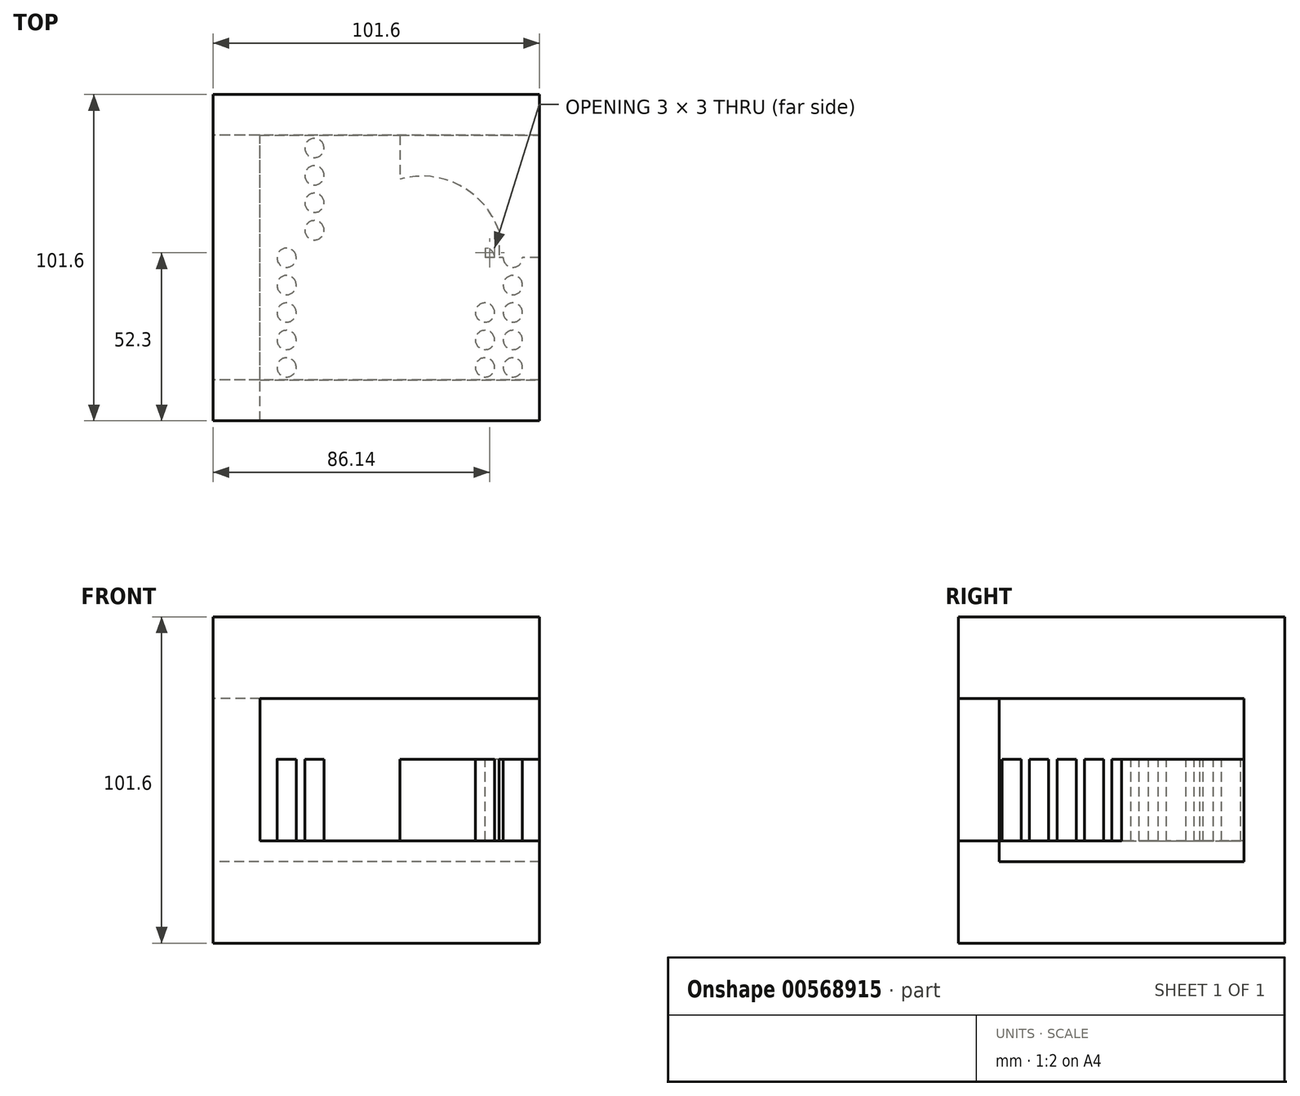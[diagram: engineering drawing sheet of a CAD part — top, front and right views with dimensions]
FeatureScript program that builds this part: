
annotation { "Feature Type Name" : "Feature", "Feature Type Description" : "" }
export const myFeature = defineFeature(function(context is Context, id is Id, definition is map)
    precondition{}
    {
        {
            var Q0;
            Q0=qCreatedBy(makeId("Front.planeOp"),FACE);
            var sketch = newSketch(context, id + "F0", { "sketchPlane" : qUnion([Q0])});
            skLineSegment(sketch, "E0.bottom", {"start": v(-50.8, 50.8) * mm, "end": v(50.8, 50.8) * mm});
            skLineSegment(sketch, "E0.top", {"start": v(-50.8, -50.8) * mm, "end": v(50.8, -50.8) * mm});
            skLineSegment(sketch, "E0.left", {"start": v(-50.8, 50.8) * mm, "end": v(-50.8, -50.8) * mm});
            skLineSegment(sketch, "E0.right", {"start": v(50.8, 50.8) * mm, "end": v(50.8, -50.8) * mm});
            skPoint(sketch, "E0.middle", {"position": v(0, 0) * mm});
            skSolve(sketch);
        }
        {
            var Q0;
            Q0=makeQuery(id+"F0.imprint","IMPRINT",FACE,{"disambiguationData":[TD([[makeQuery(id+"F0.imprint","IMPRINT",EDGE,{"derivedFrom":sQuery(id+"F0.wireOp",EDGE,"E0.bottom")}),-1.0]])]});
            extrude(context, id + "F1", {"entities" : qUnion([Q0]), "endBound" : BoundingType.SYMMETRIC, "depth" : 101.6 * mm, "offsetDistance" : 25.4 * mm});
        }
        {
            var Q0;
            Q0=qCreatedBy(makeId("Right.planeOp"),FACE);
            var sketch = newSketch(context, id + "F2", { "sketchPlane" : qUnion([Q0])});
            skLineSegment(sketch, "E1.bottom", {"start": v(-38.1, 25.4) * mm, "end": v(38.1, 25.4) * mm});
            skLineSegment(sketch, "E1.top", {"start": v(-38.1, -25.4) * mm, "end": v(38.1, -25.4) * mm});
            skLineSegment(sketch, "E1.left", {"start": v(-38.1, 25.4) * mm, "end": v(-38.1, -25.4) * mm});
            skLineSegment(sketch, "E1.right", {"start": v(38.1, 25.4) * mm, "end": v(38.1, -25.4) * mm});
            skPoint(sketch, "E1.middle", {"position": v(0, 0) * mm});
            skSolve(sketch);
        }
        {
            var Q0;
            Q0=makeQuery(id+"F2.imprint","IMPRINT",FACE,{"disambiguationData":[TD([[makeQuery(id+"F2.imprint","IMPRINT",EDGE,{"derivedFrom":sQuery(id+"F2.wireOp",EDGE,"E1.bottom")}),-1.0]])]});
            extrude(context, id + "F3", {"entities" : qUnion([Q0]), "endBound" : BoundingType.SYMMETRIC, "depth" : 101.6 * mm, "offsetDistance" : 25.4 * mm});
        }
        {
            var Q0;
            Q0=makeQuery(id+"F3.opExtrude","SWEPT_FACE",FACE,{"disambiguationData":[OSD([sQuery(id+"F2.wireOp",EDGE,"E1.right")])]});
            var sketch = newSketch(context, id + "F4", { "sketchPlane" : qUnion([Q0])});
            skLineSegment(sketch, "E2.bottom", {"start": v(36.24, 6.44) * mm, "end": v(-137.84, 6.44) * mm});
            skLineSegment(sketch, "E2.top", {"start": v(36.24, 44.36) * mm, "end": v(-137.84, 44.36) * mm});
            skLineSegment(sketch, "E2.left", {"start": v(36.24, 6.44) * mm, "end": v(36.24, 44.36) * mm});
            skLineSegment(sketch, "E2.right", {"start": v(-137.84, 6.44) * mm, "end": v(-137.84, 44.36) * mm});
            skPoint(sketch, "E2.middle", {"position": v(-50.8, 25.4) * mm});
            skSolve(sketch);
        }
        {
            var Q0;
            {var subQ0=sQuery(id+"F4.wireOp",EDGE,"E2.left");var subQ1=sQuery(id+"F4.wireOp",EDGE,"E2.bottom");var subQ2=makeQuery(id+"F4.imprint","INTERSECT",VERTEX,{"derivedFrom":[subQ1,subQ0]});Q0=makeQuery(id+"F4.imprint","IMPRINT",FACE,{"disambiguationData":[TD([[makeQuery(id+"F4.imprint","IMPRINT",EDGE,{"disambiguationData":[TD([[subQ2,-1.0]])],"derivedFrom":subQ1}),-1.0]])]});}
            extrude(context, id + "F5", {"entities" : qUnion([Q0]), "operationType" : NewBodyOperationType.REMOVE, "oppositeDirection" : true, "depth" : 135.89 * mm, "offsetDistance" : 25.4 * mm});
        }
        {
            var Q0;
            Q0=makeQuery(id+"F5.boolean.opBoolean","COPY",FACE,{"derivedFrom":makeQuery(id+"F5.opExtrude","SWEPT_FACE",FACE,{"disambiguationData":[OSD([sQuery(id+"F4.wireOp",EDGE,"E2.bottom")])]})});
            var sketch = newSketch(context, id + "F6", { "sketchPlane" : qUnion([Q0])});
            skCircle(sketch, "E3", {"center": v(33.84, 25.62) * mm, "radius": 3 * mm});
            skCircle(sketch, "E4", {"center": v(33.84, 17.08) * mm, "radius": 3 * mm});
            skCircle(sketch, "E5", {"center": v(33.84, 8.54) * mm, "radius": 3 * mm});
            skLineSegment(sketch, "E6", {"start": v(38.17, 38.1) * mm, "end": v(38.17, -38.1) * mm});
            skCircle(sketch, "E7.MirrorC", {"center": v(42.5, 25.62) * mm, "radius": 3 * mm});
            skCircle(sketch, "E8.MirrorC", {"center": v(42.5, 17.08) * mm, "radius": 3 * mm});
            skCircle(sketch, "E9.MirrorC", {"center": v(42.5, 8.54) * mm, "radius": 3 * mm});
            skLineSegment(sketch, "E10", {"start": v(50.8, 0) * mm, "end": v(-36.24, 0) * mm});
            skLineSegment(sketch, "E11", {"start": v(33.84, 38.1) * mm, "end": v(33.84, -38.1) * mm});
            skCircle(sketch, "E12.MirrorC", {"center": v(33.84, -8.54) * mm, "radius": 3 * mm});
            skCircle(sketch, "E13.MirrorC", {"center": v(33.84, -17.08) * mm, "radius": 3 * mm});
            skCircle(sketch, "E14.MirrorC", {"center": v(33.84, -25.62) * mm, "radius": 3 * mm});
            skCircle(sketch, "E15.MirrorC", {"center": v(42.5, -25.62) * mm, "radius": 3 * mm});
            skCircle(sketch, "E16.MirrorC", {"center": v(42.5, -17.08) * mm, "radius": 3 * mm});
            skCircle(sketch, "E17.MirrorC", {"center": v(42.5, -8.54) * mm, "radius": 3 * mm});
            skCircle(sketch, "E18", {"center": v(33.84, 0) * mm, "radius": 3 * mm});
            skCircle(sketch, "E19.MirrorC", {"center": v(42.5, 0) * mm, "radius": 3 * mm});
            skLineSegment(sketch, "E20", {"start": v(7.28, 38.1) * mm, "end": v(7.28, -38.1) * mm});
            skCircle(sketch, "E21.MirrorC", {"center": v(-19.28, 25.62) * mm, "radius": 3 * mm});
            skCircle(sketch, "E22.MirrorC", {"center": v(-27.94, 25.62) * mm, "radius": 3 * mm});
            skCircle(sketch, "E23.MirrorC", {"center": v(-19.28, 17.08) * mm, "radius": 3 * mm});
            skCircle(sketch, "E24.MirrorC", {"center": v(-27.94, 17.08) * mm, "radius": 3 * mm});
            skCircle(sketch, "E25.MirrorC", {"center": v(-19.28, 8.54) * mm, "radius": 3 * mm});
            skCircle(sketch, "E26.MirrorC", {"center": v(-27.94, 8.54) * mm, "radius": 3 * mm});
            skCircle(sketch, "E27.MirrorC", {"center": v(-19.28, 0) * mm, "radius": 3 * mm});
            skCircle(sketch, "E28.MirrorC", {"center": v(-27.94, 0) * mm, "radius": 3 * mm});
            skCircle(sketch, "E29.MirrorC", {"center": v(-19.28, -8.54) * mm, "radius": 3 * mm});
            skCircle(sketch, "E30.MirrorC", {"center": v(-27.94, -8.54) * mm, "radius": 3 * mm});
            skCircle(sketch, "E31.MirrorC", {"center": v(-19.28, -17.08) * mm, "radius": 3 * mm});
            skCircle(sketch, "E32.MirrorC", {"center": v(-27.94, -17.08) * mm, "radius": 3 * mm});
            skCircle(sketch, "E33.MirrorC", {"center": v(-19.28, -25.62) * mm, "radius": 3 * mm});
            skCircle(sketch, "E34.MirrorC", {"center": v(-27.94, -25.62) * mm, "radius": 3 * mm});
            skCircle(sketch, "E35", {"center": v(14.2, 0) * mm, "radius": 25.4 * mm});
            skCircle(sketch, "E36", {"center": v(33.84, 34.16) * mm, "radius": 3 * mm});
            skCircle(sketch, "E37.MirrorC", {"center": v(42.5, 34.16) * mm, "radius": 3 * mm});
            skCircle(sketch, "E38.MirrorC", {"center": v(33.84, -34.16) * mm, "radius": 3 * mm});
            skCircle(sketch, "E39.MirrorC", {"center": v(42.5, -34.16) * mm, "radius": 3 * mm});
            skCircle(sketch, "E40.MirrorC", {"center": v(-19.28, 34.16) * mm, "radius": 3 * mm});
            skCircle(sketch, "E41.MirrorC", {"center": v(-27.94, 34.16) * mm, "radius": 3 * mm});
            skCircle(sketch, "E42.MirrorC", {"center": v(-19.28, -34.16) * mm, "radius": 3 * mm});
            skCircle(sketch, "E43.MirrorC", {"center": v(-27.94, -34.16) * mm, "radius": 3 * mm});
            skSolve(sketch);
        }
        {
            var Q0;
            Q0=makeQuery(id+"F6.imprint","IMPRINT",FACE,{"disambiguationData":[TD([[makeQuery(id+"F6.imprint","IMPRINT",EDGE,{"derivedFrom":sQuery(id+"F6.wireOp",EDGE,"E22.MirrorC")}),1.0]])]});
            var Q1;
            Q1=makeQuery(id+"F6.imprint","IMPRINT",FACE,{"disambiguationData":[TD([[makeQuery(id+"F6.imprint","IMPRINT",EDGE,{"derivedFrom":sQuery(id+"F6.wireOp",EDGE,"E21.MirrorC")}),-1.0]])]});
            var Q2;
            Q2=makeQuery(id+"F6.imprint","IMPRINT",FACE,{"disambiguationData":[TD([[makeQuery(id+"F6.imprint","IMPRINT",EDGE,{"derivedFrom":sQuery(id+"F6.wireOp",EDGE,"E24.MirrorC")}),1.0]])]});
            var Q3;
            Q3=makeQuery(id+"F6.imprint","IMPRINT",FACE,{"disambiguationData":[TD([[makeQuery(id+"F6.imprint","IMPRINT",EDGE,{"derivedFrom":sQuery(id+"F6.wireOp",EDGE,"E23.MirrorC")}),-1.0]])]});
            var Q4;
            Q4=makeQuery(id+"F6.imprint","IMPRINT",FACE,{"disambiguationData":[TD([[makeQuery(id+"F6.imprint","IMPRINT",EDGE,{"derivedFrom":sQuery(id+"F6.wireOp",EDGE,"E26.MirrorC")}),1.0]])]});
            var Q5;
            Q5=makeQuery(id+"F6.imprint","IMPRINT",FACE,{"disambiguationData":[TD([[makeQuery(id+"F6.imprint","IMPRINT",EDGE,{"derivedFrom":sQuery(id+"F6.wireOp",EDGE,"E25.MirrorC")}),-1.0]])]});
            var Q6;
            {var subQ0=sQuery(id+"F6.wireOp",EDGE,"E28.MirrorC");var subQ1=sQuery(id+"F6.wireOp",EDGE,"E10");var subQ2=makeQuery(id+"F6.imprint","INTERSECT",VERTEX,{"disambiguationData":[OD(0.0)],"derivedFrom":[subQ1,subQ0]});Q6=makeQuery(id+"F6.imprint","IMPRINT",FACE,{"disambiguationData":[TD([[makeQuery(id+"F6.imprint","IMPRINT",EDGE,{"disambiguationData":[TD([[subQ2,-1.0]])],"derivedFrom":subQ1}),-1.0]])]});}
            var Q7;
            {var subQ0=sQuery(id+"F6.wireOp",EDGE,"E27.MirrorC");var subQ1=sQuery(id+"F6.wireOp",EDGE,"E10");var subQ2=makeQuery(id+"F6.imprint","INTERSECT",VERTEX,{"disambiguationData":[OD(0.0)],"derivedFrom":[subQ1,subQ0]});Q7=makeQuery(id+"F6.imprint","IMPRINT",FACE,{"disambiguationData":[TD([[makeQuery(id+"F6.imprint","IMPRINT",EDGE,{"disambiguationData":[TD([[subQ2,-1.0]])],"derivedFrom":subQ1}),1.0]])]});}
            var Q8;
            {var subQ0=sQuery(id+"F6.wireOp",EDGE,"E27.MirrorC");var subQ1=sQuery(id+"F6.wireOp",EDGE,"E10");var subQ2=makeQuery(id+"F6.imprint","INTERSECT",VERTEX,{"disambiguationData":[OD(0.0)],"derivedFrom":[subQ1,subQ0]});Q8=makeQuery(id+"F6.imprint","IMPRINT",FACE,{"disambiguationData":[TD([[makeQuery(id+"F6.imprint","IMPRINT",EDGE,{"disambiguationData":[TD([[subQ2,-1.0]])],"derivedFrom":subQ1}),-1.0]])]});}
            var Q9;
            {var subQ0=sQuery(id+"F6.wireOp",EDGE,"E28.MirrorC");var subQ1=sQuery(id+"F6.wireOp",EDGE,"E10");var subQ2=makeQuery(id+"F6.imprint","INTERSECT",VERTEX,{"disambiguationData":[OD(0.0)],"derivedFrom":[subQ1,subQ0]});Q9=makeQuery(id+"F6.imprint","IMPRINT",FACE,{"disambiguationData":[TD([[makeQuery(id+"F6.imprint","IMPRINT",EDGE,{"disambiguationData":[TD([[subQ2,-1.0]])],"derivedFrom":subQ1}),1.0]])]});}
            var Q10;
            Q10=makeQuery(id+"F6.imprint","IMPRINT",FACE,{"disambiguationData":[TD([[makeQuery(id+"F6.imprint","IMPRINT",EDGE,{"derivedFrom":sQuery(id+"F6.wireOp",EDGE,"E30.MirrorC")}),-1.0]])]});
            var Q11;
            Q11=makeQuery(id+"F6.imprint","IMPRINT",FACE,{"disambiguationData":[TD([[makeQuery(id+"F6.imprint","IMPRINT",EDGE,{"derivedFrom":sQuery(id+"F6.wireOp",EDGE,"E29.MirrorC")}),1.0]])]});
            var Q12;
            Q12=makeQuery(id+"F6.imprint","IMPRINT",FACE,{"disambiguationData":[TD([[makeQuery(id+"F6.imprint","IMPRINT",EDGE,{"derivedFrom":sQuery(id+"F6.wireOp",EDGE,"E31.MirrorC")}),1.0]])]});
            var Q13;
            Q13=makeQuery(id+"F6.imprint","IMPRINT",FACE,{"disambiguationData":[TD([[makeQuery(id+"F6.imprint","IMPRINT",EDGE,{"derivedFrom":sQuery(id+"F6.wireOp",EDGE,"E34.MirrorC")}),-1.0]])]});
            var Q14;
            Q14=makeQuery(id+"F6.imprint","IMPRINT",FACE,{"disambiguationData":[TD([[makeQuery(id+"F6.imprint","IMPRINT",EDGE,{"derivedFrom":sQuery(id+"F6.wireOp",EDGE,"E33.MirrorC")}),1.0]])]});
            var Q15;
            Q15=makeQuery(id+"F6.imprint","IMPRINT",FACE,{"disambiguationData":[TD([[makeQuery(id+"F6.imprint","IMPRINT",EDGE,{"derivedFrom":sQuery(id+"F6.wireOp",EDGE,"E32.MirrorC")}),-1.0]])]});
            var Q16;
            {var subQ1=sQuery(id+"F6.wireOp",EDGE,"E4");var subQ8=sQuery(id+"F6.wireOp",EDGE,"E35");var subQ13=makeQuery(id+"F6.imprint","INTERSECT",VERTEX,{"disambiguationData":[OD(0.0)],"derivedFrom":[subQ1,subQ8]});Q16=makeQuery(id+"F6.imprint","IMPRINT",FACE,{"disambiguationData":[TD([[makeQuery(id+"F6.imprint","IMPRINT",EDGE,{"disambiguationData":[TD([[subQ13,-1.0]])],"derivedFrom":subQ1}),-1.0]])]});}
            var Q17;
            {var subQ5=sQuery(id+"F6.wireOp",EDGE,"E18");var subQ12=sQuery(id+"F6.wireOp",EDGE,"E10");var subQ13=makeQuery(id+"F6.imprint","INTERSECT",VERTEX,{"disambiguationData":[OD(1.0)],"derivedFrom":[subQ12,subQ5]});Q17=makeQuery(id+"F6.imprint","IMPRINT",FACE,{"disambiguationData":[TD([[makeQuery(id+"F6.imprint","IMPRINT",EDGE,{"disambiguationData":[TD([[subQ13,-1.0]])],"derivedFrom":subQ12}),1.0]])]});}
            var Q18;
            {var subQ0=sQuery(id+"F6.wireOp",EDGE,"E20");var subQ1=sQuery(id+"F6.wireOp",EDGE,"E10");var subQ2=makeQuery(id+"F6.imprint","INTERSECT",VERTEX,{"derivedFrom":[subQ1,subQ0]});Q18=makeQuery(id+"F6.imprint","IMPRINT",FACE,{"disambiguationData":[TD([[makeQuery(id+"F6.imprint","IMPRINT",EDGE,{"disambiguationData":[TD([[subQ2,-1.0]])],"derivedFrom":subQ1}),1.0]])]});}
            var Q19;
            {var subQ0=sQuery(id+"F6.wireOp",EDGE,"E20");var subQ1=sQuery(id+"F6.wireOp",EDGE,"E10");var subQ2=makeQuery(id+"F6.imprint","INTERSECT",VERTEX,{"derivedFrom":[subQ1,subQ0]});Q19=makeQuery(id+"F6.imprint","IMPRINT",FACE,{"disambiguationData":[TD([[makeQuery(id+"F6.imprint","IMPRINT",EDGE,{"disambiguationData":[TD([[subQ2,-1.0]])],"derivedFrom":subQ1}),-1.0]])]});}
            var Q20;
            {var subQ0=sQuery(id+"F6.wireOp",EDGE,"E11");var subQ11=sQuery(id+"F6.wireOp",EDGE,"E4");var subQ12=makeQuery(id+"F6.imprint","INTERSECT",VERTEX,{"disambiguationData":[OD(1.0)],"derivedFrom":[subQ11,subQ0]});Q20=makeQuery(id+"F6.imprint","IMPRINT",FACE,{"disambiguationData":[TD([[makeQuery(id+"F6.imprint","IMPRINT",EDGE,{"disambiguationData":[TD([[subQ12,-1.0]])],"derivedFrom":subQ11}),-1.0]])]});}
            var Q21;
            {var subQ5=sQuery(id+"F6.wireOp",EDGE,"E10");var subQ6=sQuery(id+"F6.wireOp",EDGE,"E6");var subQ7=makeQuery(id+"F6.imprint","INTERSECT",VERTEX,{"derivedFrom":[subQ6,subQ5]});Q21=makeQuery(id+"F6.imprint","IMPRINT",FACE,{"disambiguationData":[TD([[makeQuery(id+"F6.imprint","IMPRINT",EDGE,{"disambiguationData":[TD([[subQ7,-1.0]])],"derivedFrom":subQ6}),-1.0]])]});}
            var Q22;
            {var subQ0=sQuery(id+"F6.wireOp",EDGE,"E10");var subQ1=sQuery(id+"F6.wireOp",EDGE,"E6");var subQ2=makeQuery(id+"F6.imprint","INTERSECT",VERTEX,{"derivedFrom":[subQ1,subQ0]});Q22=makeQuery(id+"F6.imprint","IMPRINT",FACE,{"disambiguationData":[TD([[makeQuery(id+"F6.imprint","IMPRINT",EDGE,{"disambiguationData":[TD([[subQ2,-1.0]])],"derivedFrom":subQ1}),1.0]])]});}
            var Q23;
            {var subQ0=sQuery(id+"F6.wireOp",EDGE,"E35");var subQ1=sQuery(id+"F6.wireOp",EDGE,"E6");var subQ2=makeQuery(id+"F6.imprint","INTERSECT",VERTEX,{"disambiguationData":[OD(0.0)],"derivedFrom":[subQ1,subQ0]});Q23=makeQuery(id+"F6.imprint","IMPRINT",FACE,{"disambiguationData":[TD([[makeQuery(id+"F6.imprint","IMPRINT",EDGE,{"disambiguationData":[TD([[subQ2,-1.0]])],"derivedFrom":subQ1}),1.0]])]});}
            var Q24;
            {var subQ0=sQuery(id+"F6.wireOp",EDGE,"E35");var subQ1=sQuery(id+"F6.wireOp",EDGE,"E4");var subQ2=makeQuery(id+"F6.imprint","INTERSECT",VERTEX,{"disambiguationData":[OD(0.0)],"derivedFrom":[subQ1,subQ0]});Q24=makeQuery(id+"F6.imprint","IMPRINT",FACE,{"disambiguationData":[TD([[makeQuery(id+"F6.imprint","IMPRINT",EDGE,{"disambiguationData":[TD([[subQ2,-1.0]])],"derivedFrom":subQ1}),1.0]])]});}
            var Q25;
            {var subQ0=sQuery(id+"F6.wireOp",EDGE,"E13.MirrorC");var subQ1=sQuery(id+"F6.wireOp",EDGE,"E11");var subQ2=makeQuery(id+"F6.imprint","INTERSECT",VERTEX,{"disambiguationData":[OD(0.0)],"derivedFrom":[subQ1,subQ0]});Q25=makeQuery(id+"F6.imprint","IMPRINT",FACE,{"disambiguationData":[TD([[makeQuery(id+"F6.imprint","IMPRINT",EDGE,{"disambiguationData":[TD([[subQ2,-1.0]])],"derivedFrom":subQ1}),-1.0]])]});}
            var Q26;
            {var subQ0=sQuery(id+"F6.wireOp",EDGE,"E12.MirrorC");var subQ1=sQuery(id+"F6.wireOp",EDGE,"E11");var subQ2=makeQuery(id+"F6.imprint","INTERSECT",VERTEX,{"disambiguationData":[OD(0.0)],"derivedFrom":[subQ1,subQ0]});Q26=makeQuery(id+"F6.imprint","IMPRINT",FACE,{"disambiguationData":[TD([[makeQuery(id+"F6.imprint","IMPRINT",EDGE,{"disambiguationData":[TD([[subQ2,-1.0]])],"derivedFrom":subQ1}),-1.0]])]});}
            var Q27;
            {var subQ0=sQuery(id+"F6.wireOp",EDGE,"E12.MirrorC");var subQ1=sQuery(id+"F6.wireOp",EDGE,"E11");var subQ2=makeQuery(id+"F6.imprint","INTERSECT",VERTEX,{"disambiguationData":[OD(0.0)],"derivedFrom":[subQ1,subQ0]});Q27=makeQuery(id+"F6.imprint","IMPRINT",FACE,{"disambiguationData":[TD([[makeQuery(id+"F6.imprint","IMPRINT",EDGE,{"disambiguationData":[TD([[subQ2,-1.0]])],"derivedFrom":subQ1}),1.0]])]});}
            var Q28;
            {var subQ0=sQuery(id+"F6.wireOp",EDGE,"E11");var subQ1=sQuery(id+"F6.wireOp",EDGE,"E10");var subQ2=makeQuery(id+"F6.imprint","INTERSECT",VERTEX,{"derivedFrom":[subQ1,subQ0]});Q28=makeQuery(id+"F6.imprint","IMPRINT",FACE,{"disambiguationData":[TD([[makeQuery(id+"F6.imprint","IMPRINT",EDGE,{"disambiguationData":[TD([[subQ2,-1.0]])],"derivedFrom":subQ1}),-1.0]])]});}
            var Q29;
            {var subQ0=sQuery(id+"F6.wireOp",EDGE,"E11");var subQ1=sQuery(id+"F6.wireOp",EDGE,"E10");var subQ2=makeQuery(id+"F6.imprint","INTERSECT",VERTEX,{"derivedFrom":[subQ1,subQ0]});Q29=makeQuery(id+"F6.imprint","IMPRINT",FACE,{"disambiguationData":[TD([[makeQuery(id+"F6.imprint","IMPRINT",EDGE,{"disambiguationData":[TD([[subQ2,-1.0]])],"derivedFrom":subQ1}),1.0]])]});}
            var Q30;
            {var subQ0=sQuery(id+"F6.wireOp",EDGE,"E18");var subQ1=sQuery(id+"F6.wireOp",EDGE,"E10");var subQ2=makeQuery(id+"F6.imprint","INTERSECT",VERTEX,{"disambiguationData":[OD(0.0)],"derivedFrom":[subQ1,subQ0]});Q30=makeQuery(id+"F6.imprint","IMPRINT",FACE,{"disambiguationData":[TD([[makeQuery(id+"F6.imprint","IMPRINT",EDGE,{"disambiguationData":[TD([[subQ2,-1.0]])],"derivedFrom":subQ1}),1.0]])]});}
            var Q31;
            {var subQ0=sQuery(id+"F6.wireOp",EDGE,"E11");var subQ1=sQuery(id+"F6.wireOp",EDGE,"E5");var subQ2=makeQuery(id+"F6.imprint","INTERSECT",VERTEX,{"disambiguationData":[OD(0.0)],"derivedFrom":[subQ1,subQ0]});Q31=makeQuery(id+"F6.imprint","IMPRINT",FACE,{"disambiguationData":[TD([[makeQuery(id+"F6.imprint","IMPRINT",EDGE,{"disambiguationData":[TD([[subQ2,1.0]])],"derivedFrom":subQ1}),1.0]])]});}
            var Q32;
            {var subQ0=sQuery(id+"F6.wireOp",EDGE,"E11");var subQ1=sQuery(id+"F6.wireOp",EDGE,"E5");var subQ2=makeQuery(id+"F6.imprint","INTERSECT",VERTEX,{"disambiguationData":[OD(0.0)],"derivedFrom":[subQ1,subQ0]});Q32=makeQuery(id+"F6.imprint","IMPRINT",FACE,{"disambiguationData":[TD([[makeQuery(id+"F6.imprint","IMPRINT",EDGE,{"disambiguationData":[TD([[subQ2,-1.0]])],"derivedFrom":subQ1}),1.0]])]});}
            var Q33;
            {var subQ0=sQuery(id+"F6.wireOp",EDGE,"E18");var subQ1=sQuery(id+"F6.wireOp",EDGE,"E10");var subQ2=makeQuery(id+"F6.imprint","INTERSECT",VERTEX,{"disambiguationData":[OD(0.0)],"derivedFrom":[subQ1,subQ0]});Q33=makeQuery(id+"F6.imprint","IMPRINT",FACE,{"disambiguationData":[TD([[makeQuery(id+"F6.imprint","IMPRINT",EDGE,{"disambiguationData":[TD([[subQ2,-1.0]])],"derivedFrom":subQ1}),-1.0]])]});}
            var Q34;
            {var subQ0=sQuery(id+"F6.wireOp",EDGE,"E13.MirrorC");var subQ1=sQuery(id+"F6.wireOp",EDGE,"E11");var subQ2=makeQuery(id+"F6.imprint","INTERSECT",VERTEX,{"disambiguationData":[OD(0.0)],"derivedFrom":[subQ1,subQ0]});Q34=makeQuery(id+"F6.imprint","IMPRINT",FACE,{"disambiguationData":[TD([[makeQuery(id+"F6.imprint","IMPRINT",EDGE,{"disambiguationData":[TD([[subQ2,-1.0]])],"derivedFrom":subQ1}),1.0]])]});}
            var Q35;
            {var subQ0=sQuery(id+"F6.wireOp",EDGE,"E11");var subQ1=sQuery(id+"F6.wireOp",EDGE,"E4");var subQ2=makeQuery(id+"F6.imprint","INTERSECT",VERTEX,{"disambiguationData":[OD(1.0)],"derivedFrom":[subQ1,subQ0]});Q35=makeQuery(id+"F6.imprint","IMPRINT",FACE,{"disambiguationData":[TD([[makeQuery(id+"F6.imprint","IMPRINT",EDGE,{"disambiguationData":[TD([[subQ2,-1.0]])],"derivedFrom":subQ1}),1.0]])]});}
            var Q36;
            {var subQ0=sQuery(id+"F6.wireOp",EDGE,"E35");var subQ1=sQuery(id+"F6.wireOp",EDGE,"E10");var subQ2=makeQuery(id+"F6.imprint","INTERSECT",VERTEX,{"disambiguationData":[OD(0.0)],"derivedFrom":[subQ1,subQ0]});Q36=makeQuery(id+"F6.imprint","IMPRINT",FACE,{"disambiguationData":[TD([[makeQuery(id+"F6.imprint","IMPRINT",EDGE,{"disambiguationData":[TD([[subQ2,-1.0]])],"derivedFrom":subQ1}),1.0]])]});}
            var Q37;
            {var subQ0=sQuery(id+"F6.wireOp",EDGE,"E35");var subQ1=sQuery(id+"F6.wireOp",EDGE,"E10");var subQ2=makeQuery(id+"F6.imprint","INTERSECT",VERTEX,{"disambiguationData":[OD(0.0)],"derivedFrom":[subQ1,subQ0]});Q37=makeQuery(id+"F6.imprint","IMPRINT",FACE,{"disambiguationData":[TD([[makeQuery(id+"F6.imprint","IMPRINT",EDGE,{"disambiguationData":[TD([[subQ2,-1.0]])],"derivedFrom":subQ1}),-1.0]])]});}
            var Q38;
            Q38=makeQuery(id+"F6.imprint","IMPRINT",FACE,{"disambiguationData":[TD([[makeQuery(id+"F6.imprint","IMPRINT",EDGE,{"derivedFrom":sQuery(id+"F6.wireOp",EDGE,"E41.MirrorC")}),1.0]])]});
            var Q39;
            Q39=makeQuery(id+"F6.imprint","IMPRINT",FACE,{"disambiguationData":[TD([[makeQuery(id+"F6.imprint","IMPRINT",EDGE,{"derivedFrom":sQuery(id+"F6.wireOp",EDGE,"E40.MirrorC")}),-1.0]])]});
            var Q40;
            Q40=makeQuery(id+"F6.imprint","IMPRINT",FACE,{"disambiguationData":[TD([[makeQuery(id+"F6.imprint","IMPRINT",EDGE,{"derivedFrom":sQuery(id+"F6.wireOp",EDGE,"E43.MirrorC")}),-1.0]])]});
            var Q41;
            Q41=makeQuery(id+"F6.imprint","IMPRINT",FACE,{"disambiguationData":[TD([[makeQuery(id+"F6.imprint","IMPRINT",EDGE,{"derivedFrom":sQuery(id+"F6.wireOp",EDGE,"E42.MirrorC")}),1.0]])]});
            extrude(context, id + "F7", {"entities" : qUnion([Q0, Q1, Q2, Q3, Q4, Q5, Q6, Q7, Q8, Q9, Q10, Q11, Q12, Q13, Q14, Q15, Q16, Q17, Q18, Q19, Q20, Q21, Q22, Q23, Q24, Q25, Q26, Q27, Q28, Q29, Q30, Q31, Q32, Q33, Q34, Q35, Q36, Q37, Q38, Q39, Q40, Q41]), "operationType" : NewBodyOperationType.REMOVE, "oppositeDirection" : true, "depth" : 25.4 * mm, "offsetDistance" : 25.4 * mm});
        }
    });
